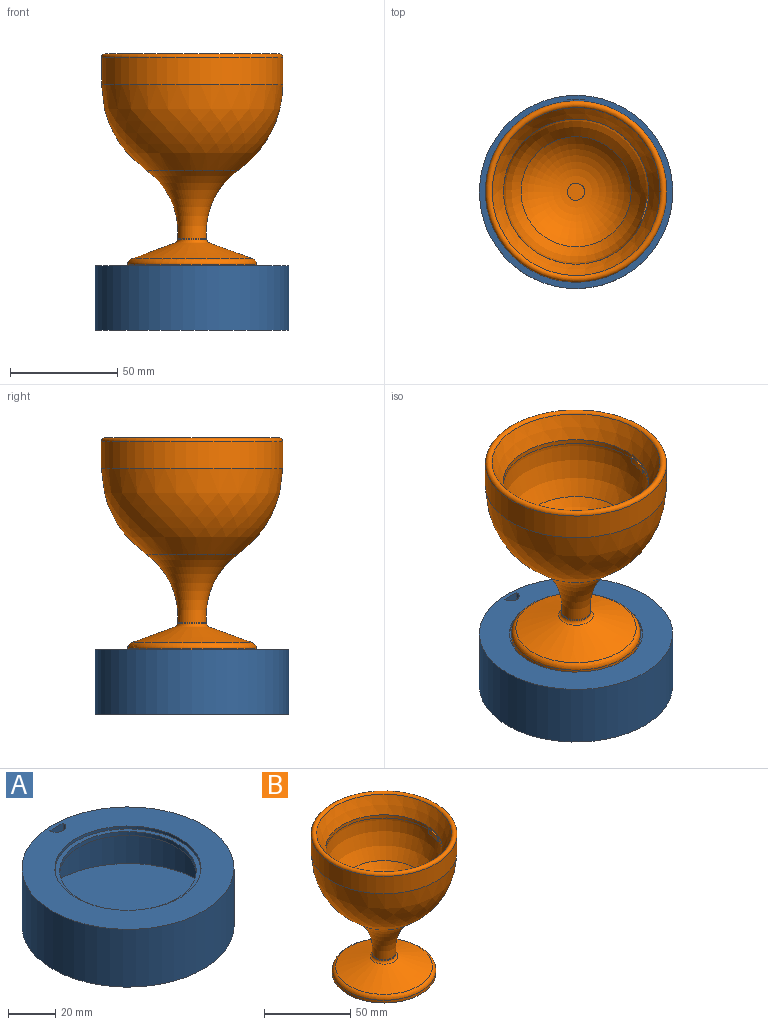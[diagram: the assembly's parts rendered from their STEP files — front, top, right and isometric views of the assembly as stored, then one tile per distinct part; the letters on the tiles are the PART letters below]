
ASSEMBLY  parts=2 mates=1
PART A: 12 faces, bbox 90x90x30 mm
  f0: cylinder r=29mm len=58mm, axis (0,0,-1), area 364.4mm2, adj f1,f8
  f1: plane 62x62mm, normal (0,0,1), area 377mm2, adj f0,f2
  f2: cylinder r=31mm len=62mm, axis (0,0,-1), area 292.2mm2, adj f1,f3
  f3: plane 90x90mm, normal (0,0,1), area 3318mm2, adj f2,f4,f9,f10
  f4: cylinder r=45mm len=90mm, axis (0,0,-1), area 8482.3mm2, adj f3,f5
  f5: plane 90x90mm, normal (0,0,-1), area 6361.7mm2, adj f4
  f6: plane 86x86mm, normal (0,0,1), area 5808.8mm2, adj f7
  f7: cylinder r=43mm len=86mm, axis (0,0,-1), area 5943.9mm2, adj f6,f8
  f8: cone r=43mm half-angle=79.9deg, axis (0,0,-1), area 3216.8mm2, adj f0,f7
  f9: cylinder r=43mm len=7.99mm, axis (0,0,1), area 40mm2, adj f3,f10,f11
  f10: cylinder r=4mm len=7.99mm, axis (0,0,1), area 61mm2, adj f3,f9,f11
  f11: plane 7.99x4mm, normal (0,0,1), area 24.6mm2, adj f9,f10
PART B: 44 faces, bbox 91.4x91.4x107.7 mm
  f0: cylinder r=33.8mm len=67.6mm, axis (0,0,1), area 457mm2, adj f1,f14,f39,f40,f41
  f1: revolved ~67.6x67.6mm, area 5105.4mm2, adj f0,f15,f40,f41,f42
  f2: cylinder r=4mm len=28.24mm, axis (0,0,1), area 642.2mm2, adj f3,f18,f21
  f3: torus R=9mm, axis (0,0,1), area 197.8mm2, adj f2,f4
  f4: cone r=20mm half-angle=70deg, axis (0,0,-1), area 1094mm2, adj f3,f19
  f5: plane 60x60mm, normal (0,0,-1), area 1503.4mm2, adj f6,f19
  f6: cylinder r=30mm len=60mm, axis (0,0,1), area 358mm2, adj f5,f20
  f7: cone r=30mm half-angle=70deg, axis (0,0,-1), area 2408.3mm2, adj f8,f20
  f8: torus R=8.75mm, axis (0,0,1), area 103.4mm2, adj f7,f9
  f9: cone r=6.76mm half-angle=5deg, axis (0,0,-1), area 21mm2, adj f8,f10
  f10: torus R=41.58mm, axis (0,0,1), area 2580.9mm2, adj f9,f11
  f11: revolved ~84.4x84.4mm, area 10353.9mm2, adj f10,f12
  f12: cylinder r=42.2mm len=84.4mm, axis (0,0,1), area 3276.4mm2, adj f11,f13
  f13: torus R=40.56mm, axis (0,0,1), area 1133.2mm2, adj f12,f14
  f14: cone r=39.08mm half-angle=25.9deg, axis (0,0,1), area 2762.9mm2, adj f0,f13
  f15: torus R=3mm, axis (0,0,1), area 2485.5mm2, adj f1,f16
  f16: cylinder r=4mm len=8mm, axis (0,0,1), area 155.9mm2, adj f15,f17,f22,f23,f24
  f17: plane 8x8mm, normal (0,0,1), area 50.3mm2, adj f16
  f18: plane 8x8mm, normal (0,0,-1), area 50.3mm2, adj f2
  f19: torus R=20.53mm, axis (0,0,-1), area 131.7mm2, adj f4,f5
  f20: torus R=27mm, axis (0,0,-1), area 674.9mm2, adj f6,f7
  f21: torus R=45mm, axis (-0.5,-0.87,0), area 445.7mm2, adj f2,f28
  f22: torus R=32.5mm, axis (0,1,0), area 512.3mm2, adj f16,f23,f24,f27
  f23: cylinder r=2.75mm len=1.5mm, axis (-1,0,0), area 0.1mm2, adj f16,f22
  f24: cylinder r=2.75mm len=1.5mm, axis (-1,0,0), area 0.1mm2, adj f16,f22
  f25: torus R=38mm, axis (0,0,1), area 0.1mm2, adj f28,f33
  f26: torus R=38mm, axis (0,0,1), area 0.1mm2, adj f27,f34
  f27: torus R=45mm, axis (0,1,0), area 464.8mm2, adj f22,f26,f30,f34,f37,f38
  f28: torus R=45mm, axis (0.5,0.87,0), area 706.8mm2, adj f21,f25,f30,f33,f35,f36
  f29: cone r=37.1mm half-angle=25.9deg, axis (0,0,1), area 767mm2, adj f30,f32,f33,f34
  f30: torus R=38mm, axis (0,0,1), area 2408.6mm2, adj f27,f28,f29,f31,f33,f34
  f31: cone r=40.47mm half-angle=25.9deg, axis (0,0,-1), area 837.5mm2, adj f30,f32,f33,f34
  f32: torus R=38mm, axis (0,0,1), area 501.4mm2, adj f29,f31,f33,f34
  f33: cylinder r=2.75mm len=8mm, axis (0,0,-1), area 42.1mm2, adj f25,f28,f29,f30,f31,f32,f35,f36
  f34: cylinder r=2.75mm len=8mm, axis (0,0,-1), area 42.1mm2, adj f26,f27,f29,f30,f31,f32,f37,f38
  f35: plane 3.88x1.5mm, normal (0,0,-1), area 0.3mm2, adj f28,f33,f36
  f36: plane 3x0.09mm, normal (-0.5,-0.87,0), area 0.1mm2, adj f28,f33,f35
  f37: plane 2.88x2.83mm, normal (0,0,-1), area 0.3mm2, adj f27,f34,f38
  f38: plane 3x0.11mm, normal (0,1,0), area 0.1mm2, adj f27,f34,f37
  f39: plane 9.98x3.38mm, normal (0,0,1), area 8.1mm2, adj f0,f40,f41,f43
  f40: plane 3x0.73mm, normal (-0.4,-0.92,0), area 2.4mm2, adj f0,f1,f39,f42,f43
  f41: plane 3x0.8mm, normal (0.11,0.99,0), area 2.4mm2, adj f0,f1,f39,f42,f43
  f42: plane 9.97x3.36mm, normal (0,0,-1), area 7.8mm2, adj f1,f40,f41,f43
  f43: cylinder r=33mm len=9.66mm, axis (0,0,-1), area 30.1mm2, adj f39,f40,f41,f42
PLACE A t=(-7.88,-28.09,5.32)mm
PLACE B t=(-7.88,-28.09,49.82)mm
MATE fastened B.f19 <-> A.f0  axis (0,0,-1) through (-7.88,-28.09,3.82)mm
